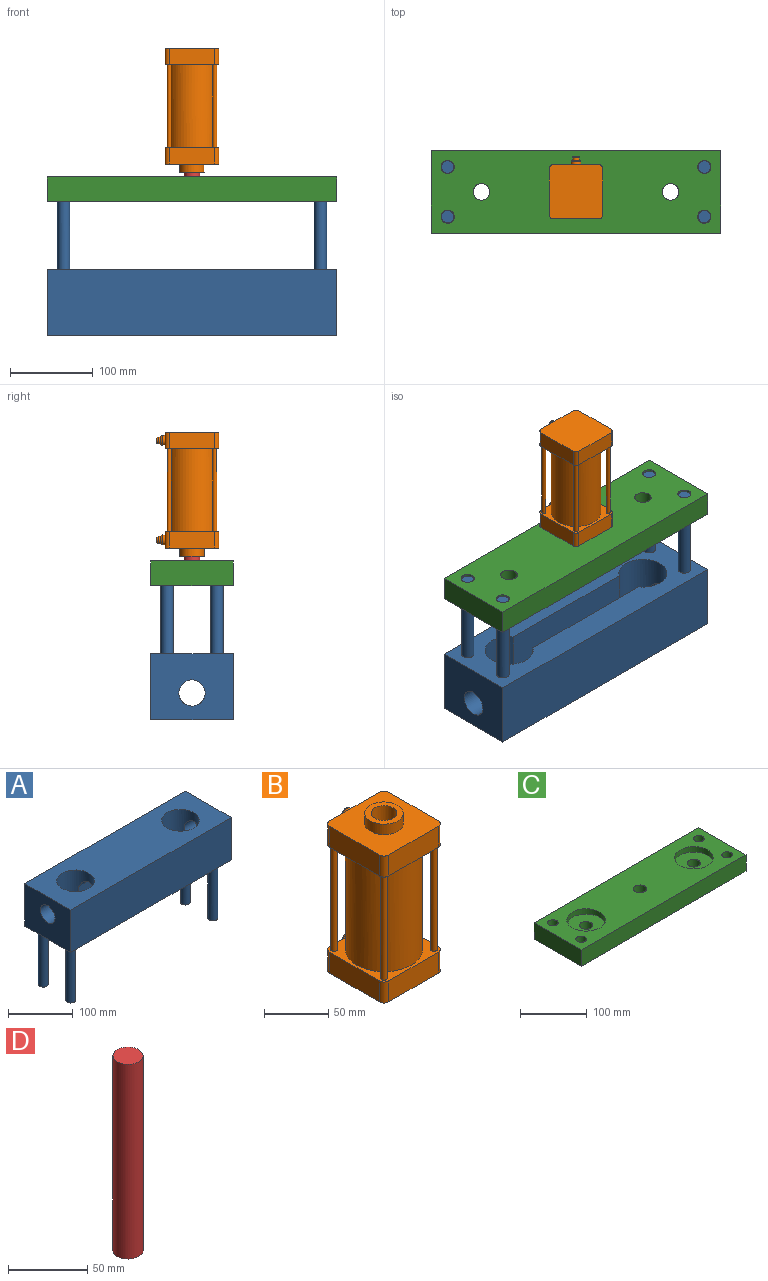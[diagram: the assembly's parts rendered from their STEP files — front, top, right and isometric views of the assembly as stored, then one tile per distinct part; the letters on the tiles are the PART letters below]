
ASSEMBLY  parts=4 mates=4
PART A: 23 faces, bbox 350x100x190 mm
  f0: cylinder r=29mm len=80mm, axis (0,0,-1), area 11663.5mm2, adj f2,f3,f8,f10,f19,f20,f21,f22
  f1: cylinder r=29mm len=80mm, axis (0,0,-1), area 11662.8mm2, adj f2,f3,f8,f9,f19,f20,f21,f22
  f2: plane 350x100mm, normal (0,0,-1), area 23270.2mm2, adj f0,f1,f4,f5,f6,f7,f11,f13
  f3: cylinder r=15.9mm len=179.84mm, axis (1,0,0), area 7849.8mm2, adj f0,f1,f19,f21
  f4: plane 100x80mm, normal (-1,0,0), area 7205.8mm2, adj f2,f5,f7,f8,f10
  f5: plane 350x80mm, normal (0,-1,0), area 28000mm2, adj f2,f4,f6,f8
  f6: plane 100x80mm, normal (1,0,0), area 7205.8mm2, adj f2,f5,f7,f8,f9
  f7: plane 350x80mm, normal (0,1,0), area 28000mm2, adj f2,f4,f6,f8
  f8: plane 350x100mm, normal (0,0,1), area 29715.8mm2, adj f0,f1,f4,f5,f6,f7
  f9: cylinder r=15.9mm len=36.45mm, axis (1,0,0), area 3398.5mm2, adj f1,f6
  f10: cylinder r=15.9mm len=36.45mm, axis (1,0,0), area 3398.8mm2, adj f0,f4
  f11: cylinder r=7.5mm len=110mm, axis (0,0,1), area 5183.6mm2, adj f2,f12
  f12: plane 15x15mm, normal (0,0,-1), area 176.7mm2, adj f11
  f13: cylinder r=7.5mm len=110mm, axis (0,0,1), area 5183.6mm2, adj f2,f14
  f14: plane 15x15mm, normal (0,0,-1), area 176.7mm2, adj f13
  f15: cylinder r=7.5mm len=110mm, axis (0,0,1), area 5183.6mm2, adj f2,f16
  f16: plane 15x15mm, normal (0,0,-1), area 176.7mm2, adj f15
  f17: cylinder r=7.5mm len=110mm, axis (0,0,1), area 5183.6mm2, adj f2,f18
  f18: plane 15x15mm, normal (0,0,-1), area 176.7mm2, adj f17
  f19: plane 180.9x0.8mm, normal (0,0,-1), area 143.9mm2, adj f0,f1,f3,f20
  f20: plane 180.9x50mm, normal (0,1,0), area 9045.2mm2, adj f0,f1,f2,f19
  f21: plane 180.9x0.8mm, normal (0,0,-1), area 143.9mm2, adj f0,f1,f3,f22
  f22: plane 180.9x50mm, normal (0,-1,0), area 9045.2mm2, adj f0,f1,f2,f21
PART B: 47 faces, bbox 65x75x150 mm
  f0: plane 40x40mm, normal (0,0,1), area 1256.6mm2, adj f2
  f1: plane 40x40mm, normal (0,0,-1), area 942.5mm2, adj f2,f3
  f2: cylinder r=20mm len=100mm, axis (0,0,1), area 12566.4mm2, adj f0,f1
  f3: cylinder r=10mm len=30mm, axis (0,0,1), area 1885mm2, adj f1,f46
  f4: cylinder r=30mm len=100mm, axis (0,0,1), area 18849.6mm2, adj f13,f25
  f5: cylinder r=5mm len=20mm, axis (0,0,1), area 157.1mm2, adj f6,f12,f13,f14
  f6: plane 55x20mm, normal (0,-1,0), area 1100mm2, adj f5,f7,f13,f14
  f7: cylinder r=5mm len=20mm, axis (0,0,1), area 157.1mm2, adj f6,f8,f13,f14
  f8: plane 55x20mm, normal (-1,0,0), area 1100mm2, adj f7,f9,f13,f14
  f9: cylinder r=5mm len=20mm, axis (0,0,1), area 157.1mm2, adj f8,f10,f13,f14
  f10: plane 55x20mm, normal (0,1,0), area 986.9mm2, adj f9,f11,f13,f14,f16
  f11: cylinder r=5mm len=20mm, axis (0,0,1), area 157.1mm2, adj f10,f12,f13,f14
  f12: plane 55x20mm, normal (1,0,0), area 1100mm2, adj f5,f11,f13,f14
  f13: plane 65x65mm, normal (0,0,-1), area 1297.6mm2, adj f4,f5,f6,f7,f8,f9,f10,f11
  f14: plane 65x65mm, normal (0,0,1), area 3496.7mm2, adj f5,f6,f7,f8,f9,f10,f11,f12
  f15: plane 9x9mm, normal (0,1,0), area 13.4mm2, adj f34,f40
  f16: cylinder r=6mm len=12mm, axis (0,-1,0), area 131.9mm2, adj f10,f40
  f17: cylinder r=5mm len=20mm, axis (0,0,-1), area 157.1mm2, adj f18,f24,f25,f26
  f18: plane 55x20mm, normal (1,0,0), area 1100mm2, adj f17,f19,f25,f26
  f19: cylinder r=5mm len=20mm, axis (0,0,-1), area 157.1mm2, adj f18,f20,f25,f26
  f20: plane 55x20mm, normal (0,1,0), area 986.9mm2, adj f19,f21,f25,f26,f27
  f21: cylinder r=5mm len=20mm, axis (0,0,-1), area 157.1mm2, adj f20,f22,f25,f26
  f22: plane 55x20mm, normal (-1,0,0), area 1100mm2, adj f21,f23,f25,f26
  f23: cylinder r=5mm len=20mm, axis (0,0,-1), area 157.1mm2, adj f22,f24,f25,f26
  f24: plane 55x20mm, normal (0,-1,0), area 1100mm2, adj f17,f23,f25,f26
  f25: plane 65x65mm, normal (0,0,1), area 1297.6mm2, adj f4,f17,f18,f19,f20,f21,f22,f23
  f26: plane 65x65mm, normal (0,0,-1), area 4203.5mm2, adj f17,f18,f19,f20,f21,f22,f23,f24
  f27: cylinder r=6mm len=12mm, axis (0,-1,0), area 131.9mm2, adj f20,f38
  f28: plane 9x9mm, normal (0,1,0), area 13.4mm2, adj f30,f38
  f29: plane 5x5mm, normal (0,1,0), area 16.5mm2, adj f31,f37
  f30: cylinder r=4mm len=8mm, axis (0,-1,0), area 88mm2, adj f28,f37
  f31: cylinder r=1mm len=10mm, axis (0,-1,0), area 62.8mm2, adj f29,f32
  f32: plane 2x2mm, normal (0,1,0), area 3.1mm2, adj f31
  f33: plane 5x5mm, normal (0,1,0), area 16.5mm2, adj f35,f39
  f34: cylinder r=4mm len=8mm, axis (0,-1,0), area 88mm2, adj f15,f39
  f35: cylinder r=1mm len=10mm, axis (0,-1,0), area 62.8mm2, adj f33,f36
  f36: plane 2x2mm, normal (0,1,0), area 3.1mm2, adj f35
  f37: torus R=2.5mm, axis (0,1,0), area 51.1mm2, adj f29,f30
  f38: torus R=4.5mm, axis (0,1,0), area 80.8mm2, adj f27,f28
  f39: torus R=2.5mm, axis (0,1,0), area 51.1mm2, adj f33,f34
  f40: torus R=4.5mm, axis (0,1,0), area 80.8mm2, adj f15,f16
  f41: cylinder r=2.5mm len=100mm, axis (0,0,1), area 1570.8mm2, adj f13,f25
  f42: cylinder r=2.5mm len=100mm, axis (0,0,1), area 1570.8mm2, adj f13,f25
  f43: cylinder r=2.5mm len=100mm, axis (0,0,1), area 1570.8mm2, adj f13,f25
  f44: cylinder r=2.5mm len=100mm, axis (0,0,1), area 1570.8mm2, adj f13,f25
  f45: cylinder r=15mm len=30mm, axis (0,0,-1), area 942.5mm2, adj f14,f46
  f46: plane 30x30mm, normal (0,0,1), area 392.7mm2, adj f3,f45
PART C: 17 faces, bbox 350x100x30 mm
  f0: plane 100x30mm, normal (-1,0,0), area 3000mm2, adj f1,f5,f6,f9
  f1: plane 350x30mm, normal (0,-1,0), area 10500mm2, adj f0,f2,f6,f9
  f2: plane 100x30mm, normal (1,0,0), area 3000mm2, adj f1,f5,f6,f9
  f3: cylinder r=29mm len=58mm, axis (0,0,1), area 1822.1mm2, adj f6,f7
  f4: cylinder r=29mm len=58mm, axis (0,0,1), area 1822.1mm2, adj f6,f8
  f5: plane 350x30mm, normal (0,1,0), area 10500mm2, adj f0,f2,f6,f9
  f6: plane 350x100mm, normal (0,0,1), area 28597.4mm2, adj f0,f1,f2,f3,f4,f5,f12,f13
  f7: plane 58x58mm, normal (0,0,1), area 2327.9mm2, adj f3,f10
  f8: plane 58x58mm, normal (0,0,1), area 2327.9mm2, adj f4,f11
  f9: plane 350x100mm, normal (0,0,-1), area 33253.3mm2, adj f0,f1,f2,f5,f10,f11,f12,f13
  f10: cylinder r=10mm len=20mm, axis (0,0,1), area 1256.6mm2, adj f7,f9
  f11: cylinder r=10mm len=20mm, axis (0,0,1), area 1256.6mm2, adj f8,f9
  f12: cylinder r=8mm len=30mm, axis (0,0,1), area 1508mm2, adj f6,f9
  f13: cylinder r=8mm len=30mm, axis (0,0,1), area 1508mm2, adj f6,f9
  f14: cylinder r=8mm len=30mm, axis (0,0,1), area 1508mm2, adj f6,f9
  f15: cylinder r=8mm len=30mm, axis (0,0,1), area 1508mm2, adj f6,f9
  f16: cylinder r=10mm len=30mm, axis (0,0,1), area 1885mm2, adj f6,f9
PART D: 3 faces, bbox 19x19x150 mm
  f0: cylinder r=9.5mm len=150mm, axis (0,0,-1), area 8953.5mm2, adj f1,f2
  f1: plane 19x19mm, normal (0,0,1), area 283.5mm2, adj f0
  f2: plane 19x19mm, normal (0,0,-1), area 283.5mm2, adj f0
PLACE A rot(axis=(0,1,0),180deg) t=(482.5,159.8,369.07)mm
PLACE B rot(axis=(0,-1,0),180deg) t=(237.69,161.37,566.52)mm
PLACE C rot(axis=(0,1,0),180deg) t=(412.69,111.37,450.97)mm
PLACE D t=(237.69,161.37,450.97)mm
MATE slider D.f0 <-> C.f16  axis (0,0,-1) through (237.69,161.37,450.97)mm
MATE slider D.f0 <-> B.f2  axis (0,0,1) through (237.69,161.37,600.97)mm
MATE fastened C.f16 <-> D.f0  axis (0,0,-1) through (237.69,161.37,450.97)mm
MATE slider A.f17 <-> C.f14  axis (0,0,1) through (82.69,191.37,479.07)mm
